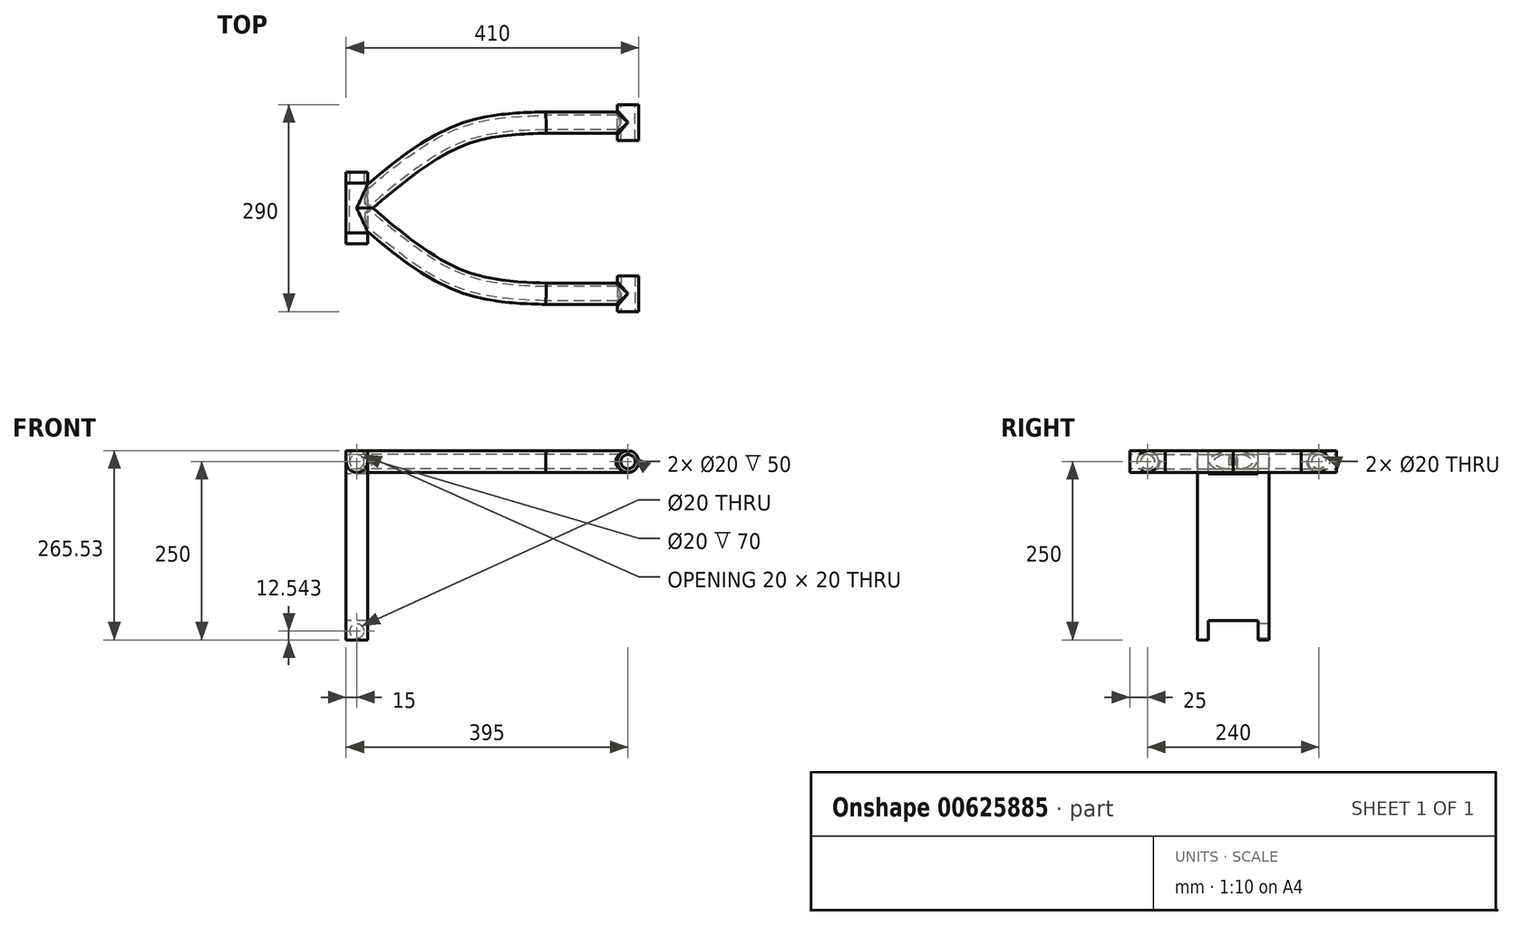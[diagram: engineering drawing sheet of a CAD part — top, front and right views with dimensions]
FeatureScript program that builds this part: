
annotation { "Feature Type Name" : "Feature", "Feature Type Description" : "" }
export const myFeature = defineFeature(function(context is Context, id is Id, definition is map)
    precondition{}
    {
        {
            var Q0;
            Q0=qCreatedBy(makeId("Front.planeOp"),FACE);
            var sketch = newSketch(context, id + "F0", { "sketchPlane" : qUnion([Q0])});
            skCircle(sketch, "E0", {"center": v(0, 0) * mm, "radius": 15 * mm});
            skCircle(sketch, "E1", {"center": v(0, 0) * mm, "radius": 10 * mm});
            skLineSegment(sketch, "E2", {"start": v(-15, 31.18) * mm, "end": v(-15, -34.32) * mm, "construction": true});
            skSolve(sketch);
        }
        {
            var Q0;
            Q0=makeQuery(id+"F0.imprint","IMPRINT",FACE,{"disambiguationData":[TD([[makeQuery(id+"F0.imprint","IMPRINT",EDGE,{"derivedFrom":sQuery(id+"F0.wireOp",EDGE,"E0")}),1.0]])]});
            extrude(context, id + "F1", {"entities" : qUnion([Q0]), "depth" : 50 * mm});
        }
        {
            var Q0;
            Q0=qCreatedBy(makeId("Right.planeOp"),FACE);
            var sketch = newSketch(context, id + "F2", { "sketchPlane" : qUnion([Q0])});
            skLineSegment(sketch, "E3", {"start": v(0, -15) * mm, "end": v(-50, -15) * mm});
            skLineSegment(sketch, "E4", {"start": v(-50, 15) * mm, "end": v(0, 15) * mm});
            skCircle(sketch, "E5", {"center": v(-25, 0) * mm, "radius": 15 * mm});
            skPoint(sketch, "E5.centerSnap0", {"position": v(-25, 15) * mm});
            skCircle(sketch, "E6", {"center": v(-25, 0) * mm, "radius": 10 * mm});
            skSolve(sketch);
        }
        {
            var Q0;
            Q0=qCreatedBy(makeId("Top.planeOp"),FACE);
            var sketch = newSketch(context, id + "F3", { "sketchPlane" : qUnion([Q0])});
            skLineSegment(sketch, "E7", {"start": v(0, -37.06) * mm, "end": v(0, -397.44) * mm, "construction": true});
            skLineSegment(sketch, "E8", {"start": v(-380, 0) * mm, "end": v(-380, -571.82) * mm, "construction": true});
            skLineSegment(sketch, "E9", {"start": v(76.72, -145) * mm, "end": v(-436.32, -145) * mm, "construction": true});
            skLineSegment(sketch, "E10", {"start": v(0, -25.32) * mm, "end": v(-114.87, -25.32) * mm});
            skFitSpline(sketch, "E11", {"points": [v(-114.87, -25.32) * mm, v(-237.42, -44.08) * mm, v(-380, -145) * mm], "startDerivative": vector(-269.22, -7.9) * mm, "endDerivative": vector(-261.26, -225.26) * mm});
            skLineSegment(sketch, "E12.MirrorCS", {"start": v(0, -264.68) * mm, "end": v(-114.87, -264.68) * mm});
            skFitSpline(sketch, "E13.MirrorCS", {"points": [v(-114.87, -264.68) * mm, v(-237.42, -245.92) * mm, v(-380, -145) * mm], "startDerivative": vector(-269.22, 7.9) * mm, "endDerivative": vector(-261.26, 225.26) * mm});
            skSolve(sketch);
        }
        {
            var Q0;
            Q0=qSketchRegion(id+"F2",true);
            var Q1;
            Q1=sQuery(id+"F3.wireOp",EDGE,"E11");
            var Q2;
            Q2=sQuery(id+"F3.wireOp",EDGE,"E10");
            sweep(context, id + "F4", {"operationType" : NewBodyOperationType.ADD, "profiles" : qUnion([Q0]), "path" : qUnion([Q1, Q2])});
        }
        {
            var Q0;
            Q0=makeQuery(id+"F4.boolean.opBoolean","INTERSECT",EDGE,{"disambiguationData":[OD(0.0)],"derivedFrom":[makeQuery(id+"F1.opExtrude","SWEPT_FACE",FACE,{"disambiguationData":[OSD([sQuery(id+"F0.wireOp",EDGE,"E0")])]}),makeQuery(id+"F4.opSweep","SWEPT_FACE",FACE,{"disambiguationData":[OSD([sQuery(id+"F2.wireOp",EDGE,"E5"),sQuery(id+"F3.wireOp",EDGE,"ba36500d-ebc8-4f5f-b360-66259673c2d1")])]})]});
            var Q1;
            Q1=makeQuery(id+"F4.boolean.opBoolean","INTERSECT",EDGE,{"disambiguationData":[OD(1.0)],"derivedFrom":[makeQuery(id+"F1.opExtrude","SWEPT_FACE",FACE,{"disambiguationData":[OSD([sQuery(id+"F0.wireOp",EDGE,"E0")])]}),makeQuery(id+"F4.opSweep","SWEPT_FACE",FACE,{"disambiguationData":[OSD([sQuery(id+"F2.wireOp",EDGE,"E5"),sQuery(id+"F3.wireOp",EDGE,"ba36500d-ebc8-4f5f-b360-66259673c2d1")])]})]});
            fillet(context, id + "F5", {"entities" : qUnion([Q0, Q1]), "radius" : 2 * mm, "tangentPropagation" : true, "allowEdgeOverflow" : false});
        }
        {
            var Q0;
            Q0=makeQuery(id+"F1.opExtrude","CAP_FACE",FACE,{"disambiguationData":[OSD([sQuery(id+"F0.wireOp",EDGE,"E0"),sQuery(id+"F0.wireOp",EDGE,"E1")])],"isStart":false});
            var sketch = newSketch(context, id + "F6", { "sketchPlane" : qUnion([Q0])});
            skCircle(sketch, "E14", {"center": v(0, 0) * mm, "radius": 10 * mm});
            skSolve(sketch);
        }
        {
            var Q0;
            Q0=qSketchRegion(id+"F6",true);
            var Q1;
            Q1=makeQuery(id+"F6.imprint","IMPRINT",FACE,{"disambiguationData":[TD([[makeQuery(id+"F6.imprint","IMPRINT",EDGE,{"derivedFrom":sQuery(id+"F6.wireOp",EDGE,"E14")}),1.0]])]});
            extrude(context, id + "F7", {"entities" : qUnion([Q0, Q1]), "operationType" : NewBodyOperationType.REMOVE, "endBound" : BoundingType.THROUGH_ALL, "oppositeDirection" : true, "depth" : 25 * mm});
        }
        {
            var Q0;
            Q0=qCreatedBy(makeId("Front.planeOp"),FACE);
            cPlane(context, id + "F8", {"entities" : qUnion([Q0]), "cplaneType" : CPlaneType.OFFSET, "offset" : 145 * mm, "width" : 150 * mm, "height" : 150 * mm});
        }
        {
            var Q0;
            Q0=makeQuery(id+"F1.opExtrude","SWEPT_BODY",BODY,{"disambiguationData":[OSD([sQuery(id+"F0.wireOp",EDGE,"E0"),sQuery(id+"F0.wireOp",EDGE,"E1")])]});
            var Q1;
            Q1=qCreatedBy(id+"F8.planeOp",FACE);
            mirror(context, id + "F9", {"operationType" : NewBodyOperationType.ADD, "entities" : qUnion([Q0]), "mirrorPlane" : qUnion([Q1])});
        }
        {
            var Q0;
            Q0=qCreatedBy(id+"F8.planeOp",FACE);
            var sketch = newSketch(context, id + "F10", { "sketchPlane" : qUnion([Q0])});
            skLineSegment(sketch, "E15", {"start": v(0, 0) * mm, "end": v(-405.9, 0) * mm, "construction": true});
            skCircle(sketch, "E16", {"center": v(-380, 0) * mm, "radius": 15 * mm});
            skCircle(sketch, "E17", {"center": v(-380, 0) * mm, "radius": 10 * mm});
            skPoint(sketch, "E18.0", {"position": v(-380, 15) * mm});
            skLineSegment(sketch, "E19", {"start": v(-380, 15) * mm, "end": v(-380, -15) * mm, "construction": true});
            skSolve(sketch);
        }
        {
            var Q0;
            Q0=qSketchRegion(id+"F10",true);
            extrude(context, id + "F11", {"entities" : qUnion([Q0]), "operationType" : NewBodyOperationType.ADD, "endBound" : BoundingType.SYMMETRIC, "depth" : 70 * mm});
        }
        {
            var Q0;
            Q0=makeQuery(id+"F11.opExtrude","CAP_FACE",FACE,{"disambiguationData":[OSD([sQuery(id+"F10.wireOp",EDGE,"E16"),sQuery(id+"F10.wireOp",EDGE,"E17")])],"isStart":false});
            var sketch = newSketch(context, id + "F12", { "sketchPlane" : qUnion([Q0])});
            skCircle(sketch, "E20", {"center": v(-380, 0) * mm, "radius": 10 * mm});
            skPoint(sketch, "E20.first.point", {"position": v(-378.85, 9.93) * mm});
            skPoint(sketch, "E20.second.point", {"position": v(-373.45, -7.56) * mm});
            skPoint(sketch, "E20.third.point", {"position": v(-388.96, -4.45) * mm});
            skSolve(sketch);
        }
        {
            var Q0;
            Q0=makeQuery(id+"F12.imprint","IMPRINT",FACE,{"disambiguationData":[TD([[makeQuery(id+"F12.imprint","IMPRINT",EDGE,{"derivedFrom":sQuery(id+"F12.wireOp",EDGE,"E20")}),1.0]])]});
            extrude(context, id + "F13", {"entities" : qUnion([Q0]), "operationType" : NewBodyOperationType.REMOVE, "endBound" : BoundingType.THROUGH_ALL, "oppositeDirection" : true, "depth" : 25 * mm});
        }
        {
            var Q0;
            Q0=makeQuery(id+"F11.opExtrude","CAP_FACE",FACE,{"disambiguationData":[OSD([sQuery(id+"F10.wireOp",EDGE,"E16"),sQuery(id+"F10.wireOp",EDGE,"E17")])],"isStart":false});
            var sketch = newSketch(context, id + "F14", { "sketchPlane" : qUnion([Q0])});
            skCircle(sketch, "E21", {"center": v(-380, 0) * mm, "radius": 10 * mm});
            skSolve(sketch);
        }
        {
            var Q0;
            Q0=makeQuery(id+"F14.imprint","IMPRINT",FACE,{"disambiguationData":[TD([[makeQuery(id+"F14.imprint","IMPRINT",EDGE,{"derivedFrom":sQuery(id+"F14.wireOp",EDGE,"E21")}),1.0]])]});
            extrude(context, id + "F15", {"entities" : qUnion([Q0]), "depth" : 100 * mm});
        }
        {
            var Q0;
            Q0=makeQuery(id+"F15.opExtrude","SWEPT_BODY",BODY,{"disambiguationData":[OSD([sQuery(id+"F14.wireOp",EDGE,"E21")])]});
            var Q1;
            {var subQ0=sQuery(id+"F10.wireOp",EDGE,"E16");var subQ1=sQuery(id+"F10.wireOp",EDGE,"E17");Q1=makeQuery(id+"F11.boolean.opBoolean","SPLIT",FACE,{"disambiguationData":[TD([makeQuery(id+"F11.opExtrude","CAP_FACE",FACE,{"disambiguationData":[OSD([subQ0,subQ1])],"isStart":true})])],"derivedFrom":makeQuery(id+"F11.opExtrude","SWEPT_FACE",FACE,{"disambiguationData":[OSD([subQ0])]})});}
            transform(context, id + "F16", {"entities" : qUnion([Q0]), "transformType" : TransformType.TRANSLATION_DISTANCE, "transformDirection" : qUnion([Q1]), "distance" : 85 * mm, "makeCopy" : false});
        }
        {
            var Q0;
            Q0=makeQuery(id+"F15.opExtrude","SWEPT_FACE",FACE,{"disambiguationData":[OSD([sQuery(id+"F14.wireOp",EDGE,"E21")])]});
            cPlane(context, id + "F17", {"entities" : qUnion([Q0]), "cplaneType" : CPlaneType.LINE_ANGLE, "offset" : 150 * mm, "angle" : 90 * degree, "width" : 150 * mm, "height" : 150 * mm});
        }
        {
            var Q0;
            Q0=qCreatedBy(id+"F17.planeOp",FACE);
            var sketch = newSketch(context, id + "F18", { "sketchPlane" : qUnion([Q0])});
            skLineSegment(sketch, "E22", {"start": v(-95, 10) * mm, "end": v(-95, -10) * mm});
            skLineSegment(sketch, "E23", {"start": v(-109.96, -16.97) * mm, "end": v(-180.1, -16.97) * mm});
            skLineSegment(sketch, "E24", {"start": v(-180.1, -16.97) * mm, "end": v(-180.1, -10) * mm});
            skLineSegment(sketch, "E25", {"start": v(-195, -10) * mm, "end": v(-195, 10) * mm});
            skLineSegment(sketch, "E26", {"start": v(-95, 0) * mm, "end": v(-195, 0) * mm, "construction": true});
            skLineSegment(sketch, "E27", {"start": v(-95, -10) * mm, "end": v(-95, -120) * mm});
            skLineSegment(sketch, "E28", {"start": v(-195, -120) * mm, "end": v(-195, -10) * mm});
            skLineSegment(sketch, "E29", {"start": v(-84.47, -120) * mm, "end": v(-204.44, -120) * mm, "construction": true});
            skLineSegment(sketch, "E30", {"start": v(-180.1, -10) * mm, "end": v(-180.1, 10) * mm});
            skLineSegment(sketch, "E31", {"start": v(-95, -120) * mm, "end": v(-195, -120) * mm});
            skLineSegment(sketch, "E32.MirrorCS", {"start": v(-95, -230) * mm, "end": v(-95, -120) * mm});
            skLineSegment(sketch, "E33.MirrorCS", {"start": v(-95, -250) * mm, "end": v(-95, -230) * mm});
            skLineSegment(sketch, "E34.MirrorCS", {"start": v(-109.96, -223.03) * mm, "end": v(-180.1, -223.03) * mm});
            skLineSegment(sketch, "E35.MirrorCS", {"start": v(-195, -230) * mm, "end": v(-195, -250) * mm});
            skLineSegment(sketch, "E36.MirrorCS", {"start": v(-195, -120) * mm, "end": v(-195, -230) * mm});
            skLineSegment(sketch, "E37", {"start": v(-95, -250) * mm, "end": v(-109.96, -250) * mm});
            skLineSegment(sketch, "E38", {"start": v(-109.96, -250) * mm, "end": v(-109.96, -223.03) * mm});
            skLineSegment(sketch, "E39", {"start": v(-180.1, -250) * mm, "end": v(-195, -250) * mm});
            skLineSegment(sketch, "E40", {"start": v(-109.96, -16.97) * mm, "end": v(-109.96, 10) * mm});
            skLineSegment(sketch, "E41", {"start": v(-95, 10) * mm, "end": v(-95, 15.53) * mm});
            skLineSegment(sketch, "E42", {"start": v(-95, 15.53) * mm, "end": v(-109.96, 15.53) * mm});
            skLineSegment(sketch, "E43", {"start": v(-180.1, 10) * mm, "end": v(-180.1, 15.47) * mm});
            skLineSegment(sketch, "E44", {"start": v(-180.1, 15.47) * mm, "end": v(-195, 15.47) * mm});
            skLineSegment(sketch, "E45", {"start": v(-195, 15.47) * mm, "end": v(-195, 10) * mm});
            skLineSegment(sketch, "E46", {"start": v(-109.96, 10) * mm, "end": v(-109.96, 15.53) * mm});
            skLineSegment(sketch, "E47", {"start": v(-180.1, -250) * mm, "end": v(-180.1, -223.03) * mm});
            skSolve(sketch);
        }
        {
            var Q0;
            Q0=makeQuery(id+"F18.imprint","IMPRINT",FACE,{"disambiguationData":[TD([[makeQuery(id+"F18.imprint","IMPRINT",EDGE,{"derivedFrom":sQuery(id+"F18.wireOp",EDGE,"E31")}),1.0]])]});
            var Q1;
            {var subQ2=sQuery(id+"F18.wireOp",EDGE,"E22");Q1=makeQuery(id+"F18.imprint","IMPRINT",FACE,{"disambiguationData":[TD([[makeQuery(id+"F18.imprint","IMPRINT",EDGE,{"derivedFrom":subQ2}),-1.0]])]});}
            extrude(context, id + "F19", {"entities" : qUnion([Q0, Q1]), "operationType" : NewBodyOperationType.ADD, "endBound" : BoundingType.SYMMETRIC, "depth" : 30 * mm});
        }
        {
            var Q0;
            Q0=makeQuery(id+"F19.opExtrude","SWEPT_FACE",FACE,{"disambiguationData":[OSD([sQuery(id+"F18.wireOp",EDGE,"E38")])]});
            var sketch = newSketch(context, id + "F20", { "sketchPlane" : qUnion([Q0])});
            skCircle(sketch, "E48", {"center": v(-380, -237.46) * mm, "radius": 10 * mm});
            skLineSegment(sketch, "E49", {"start": v(-380, -250) * mm, "end": v(-380, -224.91) * mm, "construction": true});
            skSolve(sketch);
        }
        {
            var Q0;
            Q0=makeQuery(id+"F20.imprint","IMPRINT",FACE,{"disambiguationData":[TD([[makeQuery(id+"F20.imprint","IMPRINT",EDGE,{"derivedFrom":sQuery(id+"F20.wireOp",EDGE,"E48")}),1.0]])]});
            extrude(context, id + "F21", {"entities" : qUnion([Q0]), "operationType" : NewBodyOperationType.REMOVE, "endBound" : BoundingType.THROUGH_ALL, "oppositeDirection" : true, "depth" : 25 * mm});
        }
    });
